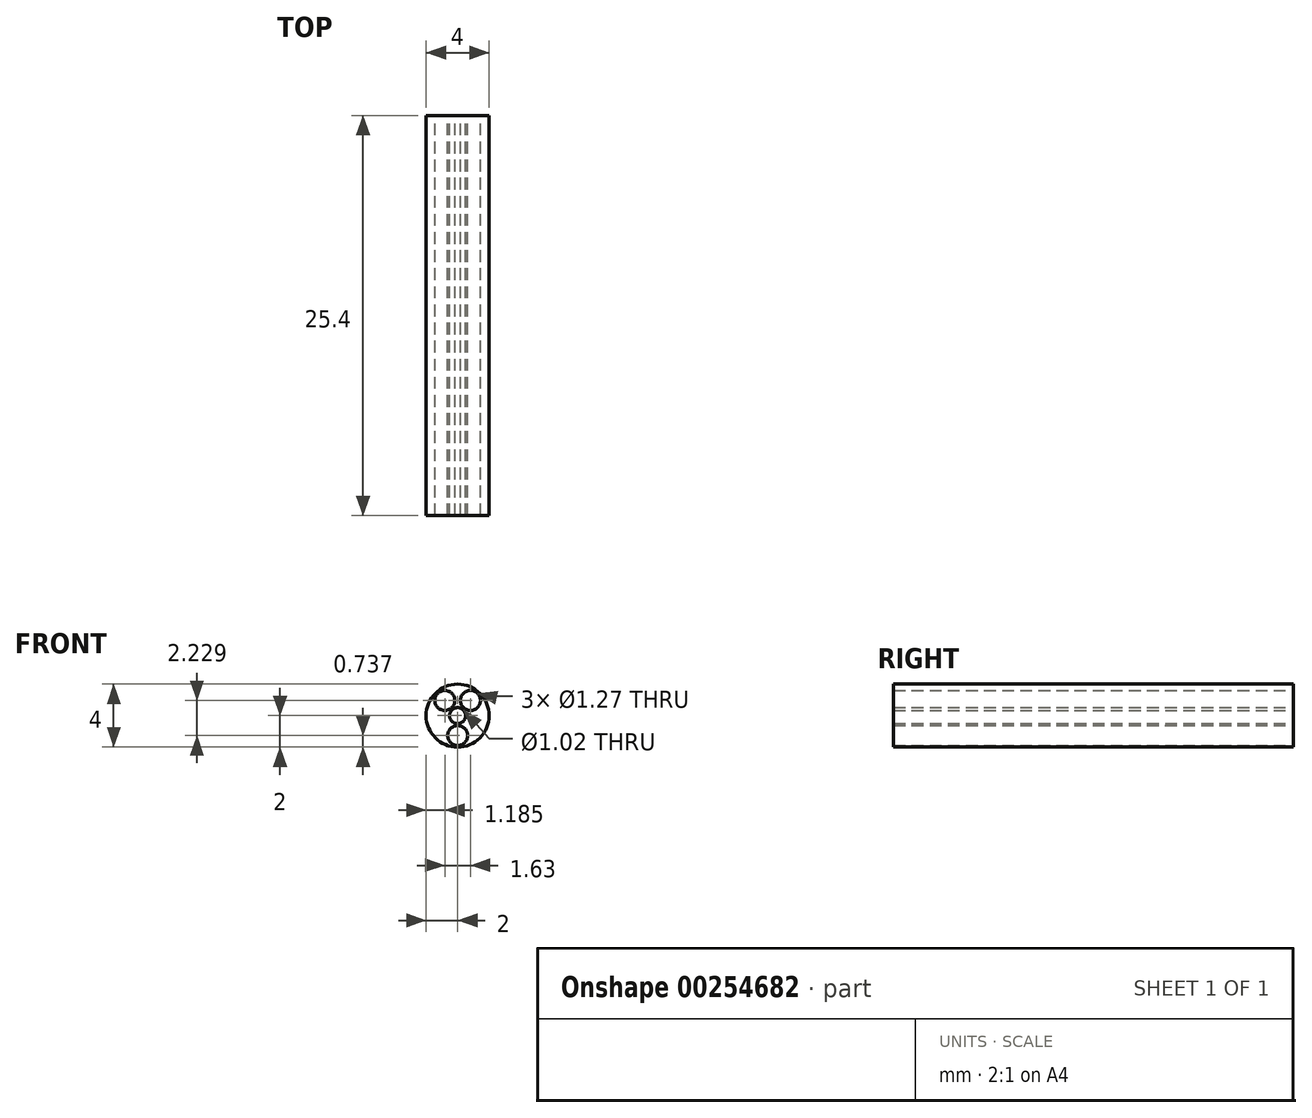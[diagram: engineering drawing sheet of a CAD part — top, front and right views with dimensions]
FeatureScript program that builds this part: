
annotation { "Feature Type Name" : "Feature", "Feature Type Description" : "" }
export const myFeature = defineFeature(function(context is Context, id is Id, definition is map)
    precondition{}
    {
        {
            var Q0;
            Q0=qCreatedBy(makeId("Front.planeOp"),FACE);
            var sketch = newSketch(context, id + "F0", { "sketchPlane" : qUnion([Q0])});
            skCircle(sketch, "E0", {"center": v(0, 0) * mm, "radius": 2 * mm});
            skCircle(sketch, "E1", {"center": v(0, 0) * mm, "radius": 0.5 * mm});
            skCircle(sketch, "E2", {"center": v(0, -1.26) * mm, "radius": 0.64 * mm});
            skCircle(sketch, "E3", {"center": v(0.82, 0.97) * mm, "radius": 0.64 * mm});
            skCircle(sketch, "E4", {"center": v(-0.82, 0.97) * mm, "radius": 0.64 * mm});
            skLineSegment(sketch, "E5", {"start": v(0, 2) * mm, "end": v(0, -2) * mm, "construction": true});
            skSolve(sketch);
        }
        {
            var Q0;
            Q0 = qSketchRegion(id + "F0", true);
            extrude(context, id + "F1", {"entities" : qUnion([Q0]), "depth" : 25.4 * mm});
        }
    });
